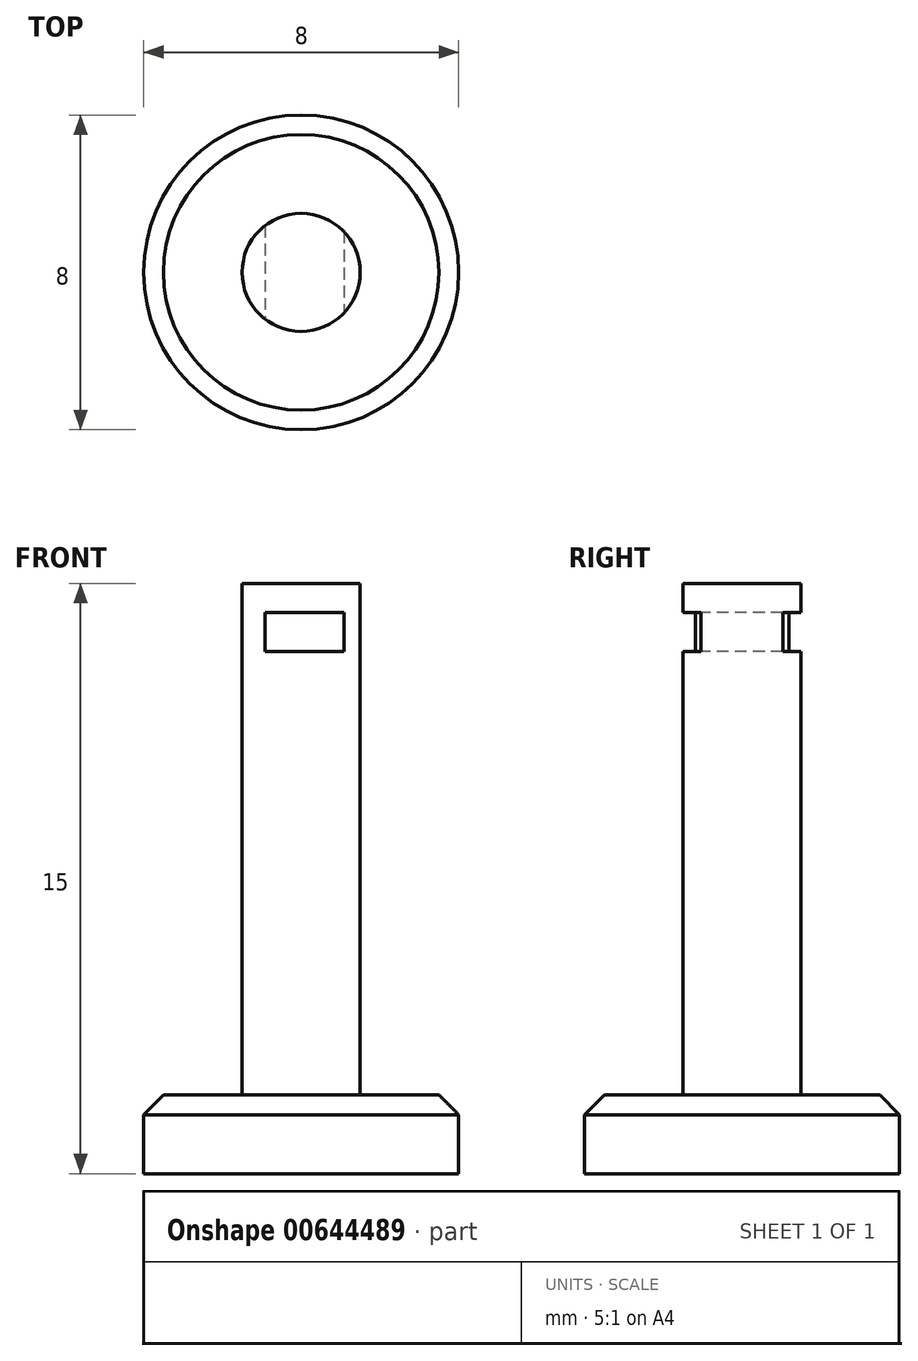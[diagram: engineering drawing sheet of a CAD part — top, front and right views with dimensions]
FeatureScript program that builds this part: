
annotation { "Feature Type Name" : "Feature", "Feature Type Description" : "" }
export const myFeature = defineFeature(function(context is Context, id is Id, definition is map)
    precondition{}
    {
        {
            var Q0;
            Q0=qCreatedBy(makeId("Top.planeOp"),FACE);
            var sketch = newSketch(context, id + "F0", { "sketchPlane" : qUnion([Q0])});
            skCircle(sketch, "E0", {"center": v(0, 0) * mm, "radius": 4 * mm});
            skCircle(sketch, "E1", {"center": v(0, 0) * mm, "radius": 1.5 * mm});
            skSolve(sketch);
        }
        {
            var Q0;
            Q0=makeQuery(id+"F0.imprint","IMPRINT",FACE,{"disambiguationData":[TD([[makeQuery(id+"F0.imprint","IMPRINT",EDGE,{"derivedFrom":sQuery(id+"F0.wireOp",EDGE,"E0")}),1.0]])]});
            extrude(context, id + "F1", {"entities" : qUnion([Q0]), "depth" : 2 * mm, "offsetDistance" : 25.4 * mm});
        }
        {
            var Q0;
            Q0=makeQuery(id+"F0.imprint","IMPRINT",FACE,{"disambiguationData":[TD([[makeQuery(id+"F0.imprint","IMPRINT",EDGE,{"derivedFrom":sQuery(id+"F0.wireOp",EDGE,"E1")}),1.0]])]});
            extrude(context, id + "F2", {"entities" : qUnion([Q0]), "operationType" : NewBodyOperationType.ADD, "depth" : 15 * mm, "offsetDistance" : 25.4 * mm});
        }
        {
            var Q0;
            Q0=makeQuery(id+"F1.opExtrude","CAP_EDGE",EDGE,{"disambiguationData":[OSD([sQuery(id+"F0.wireOp",EDGE,"E0")])],"isStart":false});
            chamfer(context, id + "F3", {"entities" : qUnion([Q0]), "width" : .5 * mm, "tangentPropagation" : true});
        }
        {
            var Q0;
            Q0=qCreatedBy(makeId("Front.planeOp"),FACE);
            var sketch = newSketch(context, id + "F4", { "sketchPlane" : qUnion([Q0])});
            skLineSegment(sketch, "E2.bottom", {"start": v(-0.92, 13.26) * mm, "end": v(1.08, 13.26) * mm});
            skLineSegment(sketch, "E2.top", {"start": v(-0.92, 14.26) * mm, "end": v(1.08, 14.26) * mm});
            skLineSegment(sketch, "E2.left", {"start": v(-0.92, 13.26) * mm, "end": v(-0.92, 14.26) * mm});
            skLineSegment(sketch, "E2.right", {"start": v(1.08, 13.26) * mm, "end": v(1.08, 14.26) * mm});
            skSolve(sketch);
        }
        {
            var Q0;
            Q0 = qSketchRegion(id + "F4", true);
            extrude(context, id + "F5", {"entities" : qUnion([Q0]), "operationType" : NewBodyOperationType.REMOVE, "endBound" : BoundingType.THROUGH_ALL, "oppositeDirection" : true, "depth" : 25.4 * mm, "offsetDistance" : 25.4 * mm});
        }
        {
            var Q0;
            Q0 = qSketchRegion(id + "F4", true);
            extrude(context, id + "F6", {"entities" : qUnion([Q0]), "operationType" : NewBodyOperationType.REMOVE, "depth" : 25.4 * mm, "offsetDistance" : 25.4 * mm});
        }
    });
